# Revit family: S-110-SL
name_source: partatom
category: Plumbing Fixtures
revit_build: Autodesk Revit MEP 2016 (Build: 20150220_1215(x64)
units: mm (PartAtom-declared; Revit-internal decimal feet)

## family parameters
Cut with Voids When Loaded = No
Host = Face
OmniClass Number = 23.45.05.17.17
OmniClass Title = Leisure Whirlpools
Part Type = Normal
Room Calculation Point = No
Round Connector Dimension = Use Diameter
Shared = Yes

## types (1)
- S-110-SL
    AHC1- Adjustable High Chair with Casters = No
    AHC2- Adjustable High Chair with Rubber Tips = No
    ARS- Arm Rest Support = No
    AS2- Adjustable Suspension Seat = No
    Amperage = 0
    CTS2- Combination Table with Side Seats = No
    CW Connection = No
    Default Elevation = 0"
    Description = S-110-S 110 Gallon S Series Stationary Whirlpool
    EG- Enviro Glaze Color Powder Coating- Specify Color (Special Finishes Consult Facrtory) = No
    GFI- Ground Fault Interrupter = No
    HW Connection = No
    Hertz = 50
    Manufacturer = Whitehall
    Material = Type 304 Stainless Steel
    Model = S-110-SL
    PCS- Pump Strainer Cover = No
    PHS2- Patient Handling System (Chair Type) = No
    RHG- Rubber Hand Grips = No
    Revised Date = 08/21/18
    S-110-SL 110 Gallon Stationary Whirlpool With Legs = Yes
    SDO- Separate Drain and Overflow Assembly = Yes
    TTS2- Tank Top Seat = No
    Tempered Water Connection = Yes
    URL = http://www.whitehallmfg.com
    Vent Connection = No
    Voltage = 115
    Waste Connection = Yes

## geometry (parser evidence)
native form markers: Sweep x18
no freeform markers — native parametric forms only
